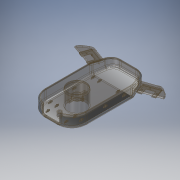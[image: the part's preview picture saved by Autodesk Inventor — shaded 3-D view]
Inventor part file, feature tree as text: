
AUTODESK INVENTOR PART (.ipt)
format: ipt  version: 2019 (Build 230136000, 136)  size: 785,408 bytes
history: native  units: mm
features: extrude x18, sketch x18, projected_geometry x8, plane x7, other x6, fillet x6, mirror x5, loft x1, shell x1, split x1, sweep x1, surface_op x1
ambient origin geometry x8: Origin, YZ Plane, XZ Plane, XY Plane, X Axis, Y Axis, Z Axis, Center Point
bodies: Body1 (feature_tree), Body2 (feature_tree), Body3 (feature_tree), Body4 (feature_tree), Body5 (feature_tree)
feature tree (73):
  other  "ROV Hull - Bottom"
  extrude  "Extrusion1"  Depth=90.0mm
  plane  "Work Plane2"
  loft  "Loft2"
  fillet  "Fillet1"  Radius=180.0mm
  fillet  "Fillet2"  [1 undecoded]
  fillet  "Fillet3"  [1 undecoded]
  fillet  "Fillet4"  Radius=60.0mm
  shell  "Shell2"  Thickness=50.0mm
  extrude  "Extrusion2"  Depth=16.0mm
  other  "Lip1"
  other  "Lip2"
  split  "Split1"
  sketch  "Sketch10"  dims[d33=50.0mm d34=16.0mm]
  extrude  "Extrusion5"  Depth=10.0mm
  extrude  "Extrusion6"  Depth=10.0mm TaperAngle=0.0deg
  sketch  "Sketch12"  dims[d47=90.0mm d48=0.0mm]
  plane  "Work Plane3"
  mirror  "Mirror1"
  plane  "Work Plane4"
  plane  "Work Plane5"
  extrude  "Extrusion12"  Depth=140.0mm TaperAngle=0.0deg
  plane  "Work Plane6"
  plane  "Work Plane7"
  extrude  "Extrusion15"  Depth=70.0mm
  extrude  "Extrusion16"  [1 undecoded]
  extrude  "Extrusion18"  TaperAngle=0.0deg  [1 undecoded]
  extrude  "Extrusion19"  Depth=25.0mm
  fillet  "Fillet8"  Radius=18.0mm
  mirror  "Mirror5"
  extrude  "Extrusion20"  Depth=5.0mm
  plane  "Work Plane8"
  extrude  "Extrusion22"  [1 undecoded]
  fillet  "Fillet10"  Radius=60.0mm
  mirror  "Mirror6"
  extrude  "Extrusion23"  Depth=57.0mm TaperAngle=0.0deg
  extrude  "Extrusion24"  Depth=2.0mm
  sweep  "Sweep1"
  extrude  "Extrusion25"  Depth=0.174533mm
  mirror  "Mirror7"
  extrude  "Extrusion26"  Depth=0.174533mm TaperAngle=0.0deg
  extrude  "Extrusion27"  Depth=3.0mm
  mirror  "Mirror8"
  extrude  "Extrusion28"  Depth=0.174533mm TaperAngle=0.0deg
  extrude  "Extrusion29"  Depth=0.174533mm
  sketch  "Sketch36"  dims[d196=65.0mm d197=0.0mm d198=17.0mm d206=4.0mm d207=0.0mm d208=3.0mm d212=11.0mm d213=0.0mm d214=100.0mm d215=12.0mm d216=0.0mm d217=90.0mm d218=5.0mm d220=13.0mm d221=0.0mm d222=0.0mm d226=10.0mm d227=6.954mm d228=6.0mm d229=6.954mm d230=6.0mm d231=5.0mm d232=0.0mm d234=6.0mm d235=70.0mm d236=0.0mm d237=6.0mm d238=5.0mm d239=8.0mm d240=0.0mm d241=0.0mm d242=52.0mm d243=46.5mm d252=10.0mm d253=10.0mm d255=12.0mm d256=0.0mm d257=4.0mm d258=11.0mm d259=0.0mm d268=0.0mm d269=10.0mm d281=20.0mm d283=2.0mm d284=2.0mm d285=10.0mm d286=0.0mm d287=1.745329mm d288=0.436332mm d289=0.0mm d290=0.0mm d291=0.0mm d292=360.0deg d293=6.6mm d294=3.0mm d295=9.5mm d296=0.349066mm d297=0.174533mm]
  other  "Boss1"
  sketch  "Sketch1"  dims[d8=250.0mm d10=90.0mm]
  sketch  "Sketch5"  dims[d11=60.0mm d12=0.0mm d22=100.0mm d24=180.0mm d26=0.0mm d27=90.0deg d28=0.0mm d29=90.0deg d30=60.0mm d32=50.0mm]
  other  "Edges1"
  projected_geometry  "Projected Loop9"
  sketch  "Sketch11"  dims[d35=10.0mm d36=360.0mm]
  projected_geometry  "Projected Loop12"
  sketch  "Sketch18"  dims[d55=10.0mm d56=4.0mm d57=0.0mm d58=0.0mm d59=0.349066mm d60=0.0mm]
  other  "Srf3"
  sketch  "Sketch20"  dims[d62=10.0mm d63=4.0mm d64=0.0mm d65=0.0mm d66=0.349066mm d67=0.0mm d77=30.0mm d78=0.0mm]
  projected_geometry  "Projected Loop19"
  projected_geometry  "Projected Loop20"
  projected_geometry  "Projected Loop25"
  sketch  "Sketch26"  dims[d83=5.0mm d84=140.0mm d85=0.0mm]
  sketch  "Sketch27"  dims[d94=-125.0mm d95=70.0mm]
  sketch  "Sketch28"  dims[d96=39.0mm d97=-405.0mm]
  sketch  "Sketch29"  dims[d124=10.0mm d125=0.0mm d133=0.0mm]
  sketch  "Sketch30"  dims[d135=344.0mm d139=25.0mm d140=18.0mm]
  sketch  "Sketch31"  dims[d143=5.0mm d144=5.0mm]
  projected_geometry  "Projected Loop28"
  sketch  "Sketch32"  dims[d162=2.5mm d173=5.0mm d174=0.0mm d175=-5.0mm d176=60.0mm d177=0.0mm]
  projected_geometry  "Projected Loop30"
  sketch  "Sketch33"  dims[d178=20.0mm d179=0.0mm d187=57.0mm d188=0.0mm]
  sketch  "Sketch34"  dims[d191=40.0mm d192=0.0mm d193=2.0mm]
  sketch  "Sketch35"  dims[d194=12.0mm d195=8.0mm]
  projected_geometry  "Projected Loop31"
  surface_op  "Boundary Patch3"
note: 5 required parameter values undecoded (feature->parameter linkage not recoverable at this tier; creation-order binding heuristic only, values carry confidence <= 0.55)
